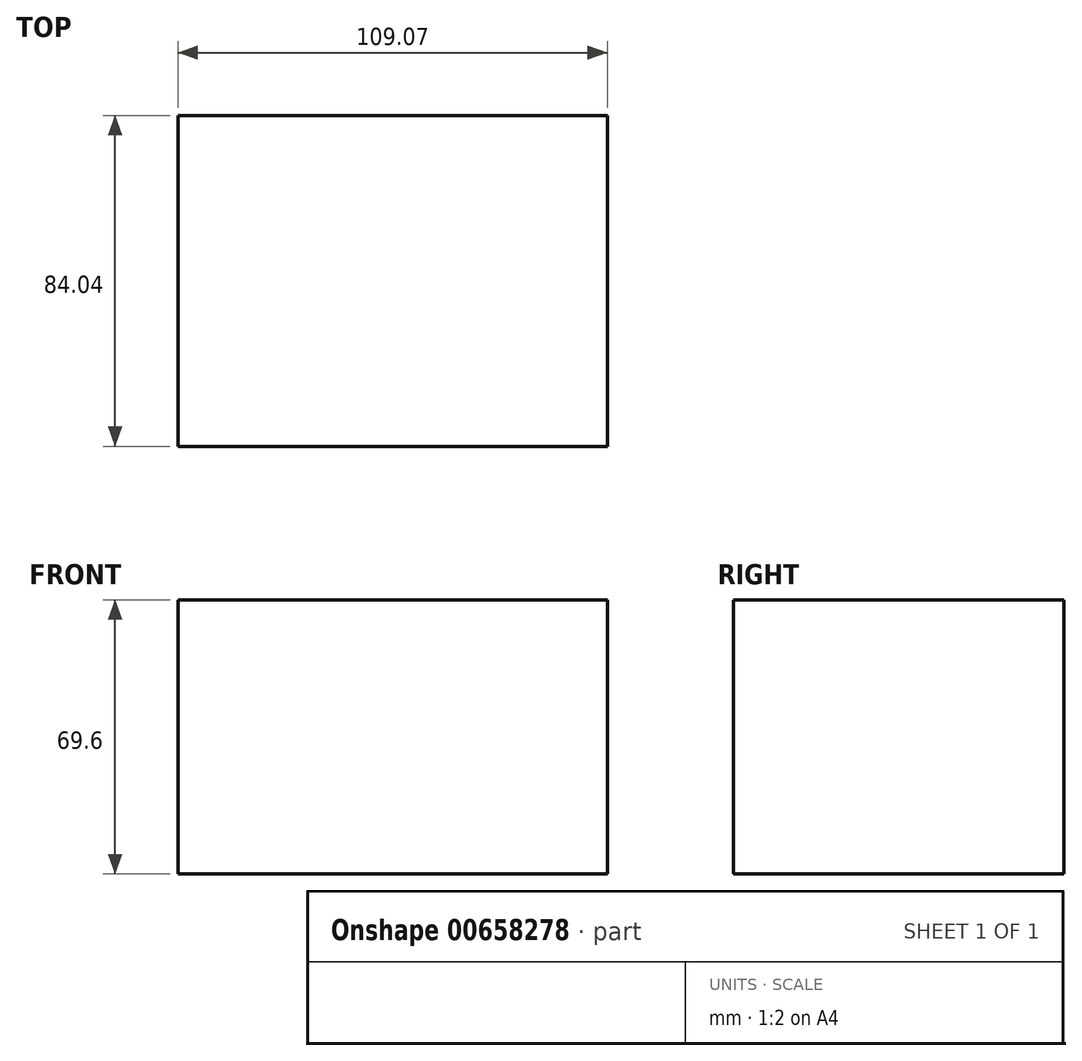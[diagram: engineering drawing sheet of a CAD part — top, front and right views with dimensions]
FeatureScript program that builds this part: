
annotation { "Feature Type Name" : "Feature", "Feature Type Description" : "" }
export const myFeature = defineFeature(function(context is Context, id is Id, definition is map)
    precondition{}
    {
        {
            var Q0;
            Q0=qCreatedBy(makeId("Top.planeOp"),FACE);
            var sketch = newSketch(context, id + "F0", { "sketchPlane" : qUnion([Q0])});
            skLineSegment(sketch, "E0.bottom", {"start": v(-76.2, -22.53) * mm, "end": v(32.87, -22.53) * mm});
            skLineSegment(sketch, "E0.top", {"start": v(-76.2, 61.5) * mm, "end": v(32.87, 61.5) * mm});
            skLineSegment(sketch, "E0.left", {"start": v(-76.2, -22.53) * mm, "end": v(-76.2, 61.5) * mm});
            skLineSegment(sketch, "E0.right", {"start": v(32.87, -22.53) * mm, "end": v(32.87, 61.5) * mm});
            skSolve(sketch);
        }
        {
            var Q0;
            Q0 = qSketchRegion(id + "F0", true);
            extrude(context, id + "F1", {"entities" : qUnion([Q0]), "depth" : 69.6 * mm, "offsetDistance" : 25.4 * mm});
        }
    });
